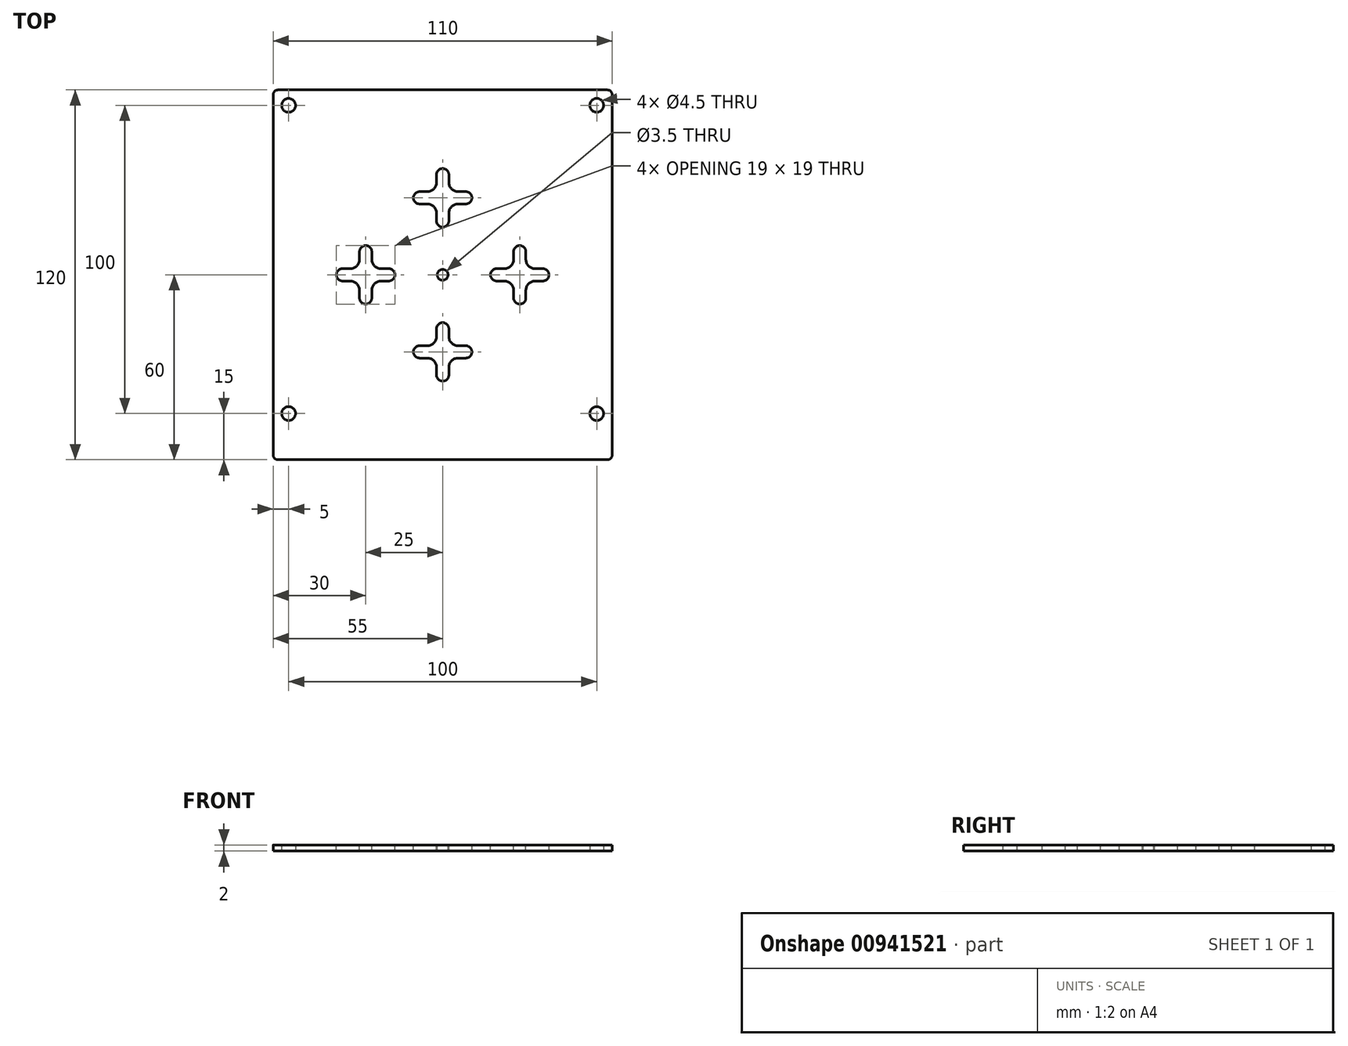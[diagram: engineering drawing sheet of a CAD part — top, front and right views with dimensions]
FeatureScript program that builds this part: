
annotation { "Feature Type Name" : "Feature", "Feature Type Description" : "" }
export const myFeature = defineFeature(function(context is Context, id is Id, definition is map)
    precondition{}
    {
        {
            var Q0;
            Q0=qCreatedBy(makeId("Top.planeOp"),FACE);
            var sketch = newSketch(context, id + "F0", { "sketchPlane" : qUnion([Q0])});
            skLineSegment(sketch, "E0.bottom", {"start": v(55, 60) * mm, "end": v(-55, 60) * mm});
            skLineSegment(sketch, "E0.top", {"start": v(55, -60) * mm, "end": v(-55, -60) * mm});
            skLineSegment(sketch, "E0.left", {"start": v(55, 60) * mm, "end": v(55, -60) * mm});
            skLineSegment(sketch, "E0.right", {"start": v(-55, 60) * mm, "end": v(-55, -60) * mm});
            skPoint(sketch, "E0.middle", {"position": v(0, 0) * mm});
            skLineSegment(sketch, "E1.bottom", {"start": v(50, 55) * mm, "end": v(-50, 55) * mm});
            skLineSegment(sketch, "E1.top", {"start": v(50, -45) * mm, "end": v(-50, -45) * mm});
            skLineSegment(sketch, "E1.left", {"start": v(50, 55) * mm, "end": v(50, -45) * mm});
            skLineSegment(sketch, "E1.right", {"start": v(-50, 55) * mm, "end": v(-50, -45) * mm});
            skPoint(sketch, "E1.middle", {"position": v(0, 5) * mm});
            skCircle(sketch, "E2", {"center": v(-50, 55) * mm, "radius": 2.25 * mm});
            skCircle(sketch, "E3", {"center": v(50, 55) * mm, "radius": 2.25 * mm});
            skCircle(sketch, "E4", {"center": v(-50, -45) * mm, "radius": 2.25 * mm});
            skCircle(sketch, "E5", {"center": v(50, -45) * mm, "radius": 2.25 * mm});
            skSolve(sketch);
        }
        {
            var Q0;
            Q0=makeQuery(id+"F0.imprint","IMPRINT",FACE,{"disambiguationData":[TD([[makeQuery(id+"F0.imprint","IMPRINT",EDGE,{"derivedFrom":sQuery(id+"F0.wireOp",EDGE,"E0.bottom")}),1.0]])]});
            var Q1;
            {var subQ5=sQuery(id+"F0.wireOp",EDGE,"E3");var subQ13=sQuery(id+"F0.wireOp",EDGE,"E1.bottom");var subQ14=makeQuery(id+"F0.imprint","INTERSECT",VERTEX,{"derivedFrom":[subQ13,subQ5]});Q1=makeQuery(id+"F0.imprint","IMPRINT",FACE,{"disambiguationData":[TD([[makeQuery(id+"F0.imprint","IMPRINT",EDGE,{"disambiguationData":[TD([[subQ14,-1.0]])],"derivedFrom":subQ13}),1.0]])]});}
            extrude(context, id + "F1", {"entities" : qUnion([Q0, Q1]), "depth" : 2 * mm, "offsetDistance" : 25 * mm});
        }
        {
            var Q0;
            Q0=makeQuery(id+"F1.opExtrude","SWEPT_EDGE",EDGE,{"disambiguationData":[OSD([sQuery(id+"F0.wireOp",EDGE,"E0.bottom"),sQuery(id+"F0.wireOp",EDGE,"E0.left")])]});
            var Q1;
            Q1=makeQuery(id+"F1.opExtrude","SWEPT_EDGE",EDGE,{"disambiguationData":[OSD([sQuery(id+"F0.wireOp",EDGE,"E0.top"),sQuery(id+"F0.wireOp",EDGE,"E0.left")])]});
            var Q2;
            Q2=makeQuery(id+"F1.opExtrude","SWEPT_EDGE",EDGE,{"disambiguationData":[OSD([sQuery(id+"F0.wireOp",EDGE,"E0.top"),sQuery(id+"F0.wireOp",EDGE,"E0.right")])]});
            var Q3;
            Q3=makeQuery(id+"F1.opExtrude","SWEPT_EDGE",EDGE,{"disambiguationData":[OSD([sQuery(id+"F0.wireOp",EDGE,"E0.bottom"),sQuery(id+"F0.wireOp",EDGE,"E0.right")])]});
            fillet(context, id + "F2", {"entities" : qUnion([Q0, Q1, Q2, Q3]), "radius" : 1.5 * mm, "tangentPropagation" : true, "allowEdgeOverflow" : false});
        }
        {
            var Q0;
            Q0=makeQuery(id+"F1.opExtrude","CAP_FACE",FACE,{"disambiguationData":[OSD([sQuery(id+"F0.wireOp",EDGE,"E0.bottom"),sQuery(id+"F0.wireOp",EDGE,"E0.top"),sQuery(id+"F0.wireOp",EDGE,"E0.left"),sQuery(id+"F0.wireOp",EDGE,"E0.right"),sQuery(id+"F0.wireOp",EDGE,"E2"),sQuery(id+"F0.wireOp",EDGE,"E3"),sQuery(id+"F0.wireOp",EDGE,"E4"),sQuery(id+"F0.wireOp",EDGE,"E5")])],"isStart":false});
            var sketch = newSketch(context, id + "F3", { "sketchPlane" : qUnion([Q0])});
            skLineSegment(sketch, "E6", {"start": v(-25, 7.5) * mm, "end": v(-25, -7.5) * mm});
            skLineSegment(sketch, "E7", {"start": v(-32.5, 0) * mm, "end": v(-17.5, 0) * mm});
            skArc(sketch, "E8.0.startCap", {"start": v(-27, 7.5) * mm, "mid": v(-25, 9.5) * mm, "end": v(-23, 7.5) * mm});
            skArc(sketch, "E8.0.endCap", {"start": v(-23, -7.5) * mm, "mid": v(-25, -9.5) * mm, "end": v(-27, -7.5) * mm});
            skLineSegment(sketch, "E8.0.left", {"start": v(-23, 7.5) * mm, "end": v(-23, -7.5) * mm});
            skLineSegment(sketch, "E8.0.right", {"start": v(-27, 7.5) * mm, "end": v(-27, -7.5) * mm});
            skArc(sketch, "E8.1.startCap", {"start": v(-32.5, -2) * mm, "mid": v(-34.5, 0) * mm, "end": v(-32.5, 2) * mm});
            skArc(sketch, "E8.1.endCap", {"start": v(-17.5, 2) * mm, "mid": v(-15.5, 0) * mm, "end": v(-17.5, -2) * mm});
            skLineSegment(sketch, "E8.1.left", {"start": v(-32.5, 2) * mm, "end": v(-17.5, 2) * mm});
            skLineSegment(sketch, "E8.1.right", {"start": v(-32.5, -2) * mm, "end": v(-17.5, -2) * mm});
            skCircle(sketch, "E9", {"center": v(0, 0) * mm, "radius": 1.75 * mm});
            skLineSegment(sketch, "E10.1.0.0", {"start": v(17.5, 2) * mm, "end": v(32.5, 2) * mm});
            skArc(sketch, "E10.1.0.1", {"start": v(17.5, -2) * mm, "mid": v(15.5, 0) * mm, "end": v(17.5, 2) * mm});
            skArc(sketch, "E10.1.0.2", {"start": v(23, 7.5) * mm, "mid": v(25, 9.5) * mm, "end": v(27, 7.5) * mm});
            skLineSegment(sketch, "E10.1.0.3", {"start": v(27, 7.5) * mm, "end": v(27, -7.5) * mm});
            skLineSegment(sketch, "E10.1.0.4", {"start": v(17.5, 0) * mm, "end": v(32.5, 0) * mm});
            skLineSegment(sketch, "E10.1.0.5", {"start": v(25, 7.5) * mm, "end": v(25, -7.5) * mm});
            skLineSegment(sketch, "E10.1.0.6", {"start": v(23, 7.5) * mm, "end": v(23, -7.5) * mm});
            skArc(sketch, "E10.1.0.7", {"start": v(32.5, 2) * mm, "mid": v(34.5, 0) * mm, "end": v(32.5, -2) * mm});
            skLineSegment(sketch, "E10.1.0.8", {"start": v(17.5, -2) * mm, "end": v(32.5, -2) * mm});
            skArc(sketch, "E10.1.0.9", {"start": v(27, -7.5) * mm, "mid": v(25, -9.5) * mm, "end": v(23, -7.5) * mm});
            skLineSegment(sketch, "E10.direction1", {"start": v(-27, -7.5) * mm, "end": v(23, -7.5) * mm, "construction": true});
            skLineSegment(sketch, "E11", {"start": v(0, 32.5) * mm, "end": v(0, 17.5) * mm});
            skLineSegment(sketch, "E12", {"start": v(-7.5, 25) * mm, "end": v(7.5, 25) * mm});
            skArc(sketch, "E13.0.startCap", {"start": v(-2, 32.5) * mm, "mid": v(0, 34.5) * mm, "end": v(2, 32.5) * mm});
            skArc(sketch, "E13.0.endCap", {"start": v(2, 17.5) * mm, "mid": v(0, 15.5) * mm, "end": v(-2, 17.5) * mm});
            skLineSegment(sketch, "E13.0.left", {"start": v(2, 32.5) * mm, "end": v(2, 17.5) * mm});
            skLineSegment(sketch, "E13.0.right", {"start": v(-2, 32.5) * mm, "end": v(-2, 17.5) * mm});
            skArc(sketch, "E13.1.startCap", {"start": v(-7.5, 23) * mm, "mid": v(-9.5, 25) * mm, "end": v(-7.5, 27) * mm});
            skArc(sketch, "E13.1.endCap", {"start": v(7.5, 27) * mm, "mid": v(9.5, 25) * mm, "end": v(7.5, 23) * mm});
            skLineSegment(sketch, "E13.1.left", {"start": v(-7.5, 27) * mm, "end": v(7.5, 27) * mm});
            skLineSegment(sketch, "E13.1.right", {"start": v(-7.5, 23) * mm, "end": v(7.5, 23) * mm});
            skArc(sketch, "E14.0.1.0", {"start": v(2, -32.5) * mm, "mid": v(0, -34.5) * mm, "end": v(-2, -32.5) * mm});
            skArc(sketch, "E14.0.1.1", {"start": v(-7.5, -27) * mm, "mid": v(-9.5, -25) * mm, "end": v(-7.5, -23) * mm});
            skLineSegment(sketch, "E14.0.1.2", {"start": v(-7.5, -25) * mm, "end": v(7.5, -25) * mm});
            skLineSegment(sketch, "E14.0.1.3", {"start": v(2, -17.5) * mm, "end": v(2, -32.5) * mm});
            skLineSegment(sketch, "E14.0.1.4", {"start": v(-7.5, -23) * mm, "end": v(7.5, -23) * mm});
            skLineSegment(sketch, "E14.0.1.5", {"start": v(0, -17.5) * mm, "end": v(0, -32.5) * mm});
            skLineSegment(sketch, "E14.0.1.6", {"start": v(-7.5, -27) * mm, "end": v(7.5, -27) * mm});
            skArc(sketch, "E14.0.1.7", {"start": v(7.5, -23) * mm, "mid": v(9.5, -25) * mm, "end": v(7.5, -27) * mm});
            skLineSegment(sketch, "E14.0.1.8", {"start": v(-2, -17.5) * mm, "end": v(-2, -32.5) * mm});
            skArc(sketch, "E14.0.1.9", {"start": v(-2, -17.5) * mm, "mid": v(0, -15.5) * mm, "end": v(2, -17.5) * mm});
            skLineSegment(sketch, "E14.direction1", {"start": v(-2, 17.5) * mm, "end": v(21, 17.5) * mm, "construction": true});
            skLineSegment(sketch, "E14.direction2", {"start": v(-2, 17.5) * mm, "end": v(-2, -32.5) * mm, "construction": true});
            skSolve(sketch);
        }
        {
            var Q0;
            Q0 = qSketchRegion(id + "F3", true);
            extrude(context, id + "F4", {"entities" : qUnion([Q0]), "operationType" : NewBodyOperationType.REMOVE, "oppositeDirection" : true, "depth" : 2 * mm, "offsetDistance" : 25 * mm});
        }
        {
            var Q0;
            Q0=makeQuery(id+"F4.boolean.opBoolean","COPY",EDGE,{"derivedFrom":makeQuery(id+"F4.opExtrude","SWEPT_EDGE",EDGE,{"disambiguationData":[OSD([sQuery(id+"F3.wireOp",EDGE,"E8.0.left"),sQuery(id+"F3.wireOp",EDGE,"E8.1.right")])]})});
            var Q1;
            Q1=makeQuery(id+"F4.boolean.opBoolean","COPY",EDGE,{"derivedFrom":makeQuery(id+"F4.opExtrude","SWEPT_EDGE",EDGE,{"disambiguationData":[OSD([sQuery(id+"F3.wireOp",EDGE,"E8.0.left"),sQuery(id+"F3.wireOp",EDGE,"E8.1.left")])]})});
            var Q2;
            Q2=makeQuery(id+"F4.boolean.opBoolean","COPY",EDGE,{"derivedFrom":makeQuery(id+"F4.opExtrude","SWEPT_EDGE",EDGE,{"disambiguationData":[OSD([sQuery(id+"F3.wireOp",EDGE,"E8.0.right"),sQuery(id+"F3.wireOp",EDGE,"E8.1.right")])]})});
            var Q3;
            Q3=makeQuery(id+"F4.boolean.opBoolean","COPY",EDGE,{"derivedFrom":makeQuery(id+"F4.opExtrude","SWEPT_EDGE",EDGE,{"disambiguationData":[OSD([sQuery(id+"F3.wireOp",EDGE,"E8.0.right"),sQuery(id+"F3.wireOp",EDGE,"E8.1.left")])]})});
            var Q4;
            Q4=makeQuery(id+"F4.boolean.opBoolean","COPY",EDGE,{"derivedFrom":makeQuery(id+"F4.opExtrude","SWEPT_EDGE",EDGE,{"disambiguationData":[OSD([sQuery(id+"F3.wireOp",EDGE,"E10.1.0.0"),sQuery(id+"F3.wireOp",EDGE,"E10.1.0.6")])]})});
            var Q5;
            Q5=makeQuery(id+"F4.boolean.opBoolean","COPY",EDGE,{"derivedFrom":makeQuery(id+"F4.opExtrude","SWEPT_EDGE",EDGE,{"disambiguationData":[OSD([sQuery(id+"F3.wireOp",EDGE,"E10.1.0.6"),sQuery(id+"F3.wireOp",EDGE,"E10.1.0.8")])]})});
            var Q6;
            Q6=makeQuery(id+"F4.boolean.opBoolean","COPY",EDGE,{"derivedFrom":makeQuery(id+"F4.opExtrude","SWEPT_EDGE",EDGE,{"disambiguationData":[OSD([sQuery(id+"F3.wireOp",EDGE,"E10.1.0.0"),sQuery(id+"F3.wireOp",EDGE,"E10.1.0.3")])]})});
            var Q7;
            Q7=makeQuery(id+"F4.boolean.opBoolean","COPY",EDGE,{"derivedFrom":makeQuery(id+"F4.opExtrude","SWEPT_EDGE",EDGE,{"disambiguationData":[OSD([sQuery(id+"F3.wireOp",EDGE,"E10.1.0.3"),sQuery(id+"F3.wireOp",EDGE,"E10.1.0.8")])]})});
            var Q8;
            Q8=makeQuery(id+"F4.boolean.opBoolean","COPY",EDGE,{"derivedFrom":makeQuery(id+"F4.opExtrude","SWEPT_EDGE",EDGE,{"disambiguationData":[OSD([sQuery(id+"F3.wireOp",EDGE,"E13.0.right"),sQuery(id+"F3.wireOp",EDGE,"E13.1.left")])]})});
            var Q9;
            Q9=makeQuery(id+"F4.boolean.opBoolean","COPY",EDGE,{"derivedFrom":makeQuery(id+"F4.opExtrude","SWEPT_EDGE",EDGE,{"disambiguationData":[OSD([sQuery(id+"F3.wireOp",EDGE,"E13.0.left"),sQuery(id+"F3.wireOp",EDGE,"E13.1.left")])]})});
            var Q10;
            Q10=makeQuery(id+"F4.boolean.opBoolean","COPY",EDGE,{"derivedFrom":makeQuery(id+"F4.opExtrude","SWEPT_EDGE",EDGE,{"disambiguationData":[OSD([sQuery(id+"F3.wireOp",EDGE,"E13.0.left"),sQuery(id+"F3.wireOp",EDGE,"E13.1.right")])]})});
            var Q11;
            Q11=makeQuery(id+"F4.boolean.opBoolean","COPY",EDGE,{"derivedFrom":makeQuery(id+"F4.opExtrude","SWEPT_EDGE",EDGE,{"disambiguationData":[OSD([sQuery(id+"F3.wireOp",EDGE,"E13.0.right"),sQuery(id+"F3.wireOp",EDGE,"E13.1.right")])]})});
            var Q12;
            Q12=makeQuery(id+"F4.boolean.opBoolean","COPY",EDGE,{"derivedFrom":makeQuery(id+"F4.opExtrude","SWEPT_EDGE",EDGE,{"disambiguationData":[OSD([sQuery(id+"F3.wireOp",EDGE,"E14.0.1.4"),sQuery(id+"F3.wireOp",EDGE,"E14.0.1.8")])]})});
            var Q13;
            Q13=makeQuery(id+"F4.boolean.opBoolean","COPY",EDGE,{"derivedFrom":makeQuery(id+"F4.opExtrude","SWEPT_EDGE",EDGE,{"disambiguationData":[OSD([sQuery(id+"F3.wireOp",EDGE,"E14.0.1.6"),sQuery(id+"F3.wireOp",EDGE,"E14.0.1.8")])]})});
            var Q14;
            Q14=makeQuery(id+"F4.boolean.opBoolean","COPY",EDGE,{"derivedFrom":makeQuery(id+"F4.opExtrude","SWEPT_EDGE",EDGE,{"disambiguationData":[OSD([sQuery(id+"F3.wireOp",EDGE,"E14.0.1.3"),sQuery(id+"F3.wireOp",EDGE,"E14.0.1.6")])]})});
            var Q15;
            Q15=makeQuery(id+"F4.boolean.opBoolean","COPY",EDGE,{"derivedFrom":makeQuery(id+"F4.opExtrude","SWEPT_EDGE",EDGE,{"disambiguationData":[OSD([sQuery(id+"F3.wireOp",EDGE,"E14.0.1.3"),sQuery(id+"F3.wireOp",EDGE,"E14.0.1.4")])]})});
            fillet(context, id + "F5", {"entities" : qUnion([Q0, Q1, Q2, Q3, Q4, Q5, Q6, Q7, Q8, Q9, Q10, Q11, Q12, Q13, Q14, Q15]), "radius" : 3 * mm, "tangentPropagation" : true, "allowEdgeOverflow" : false});
        }
    });
